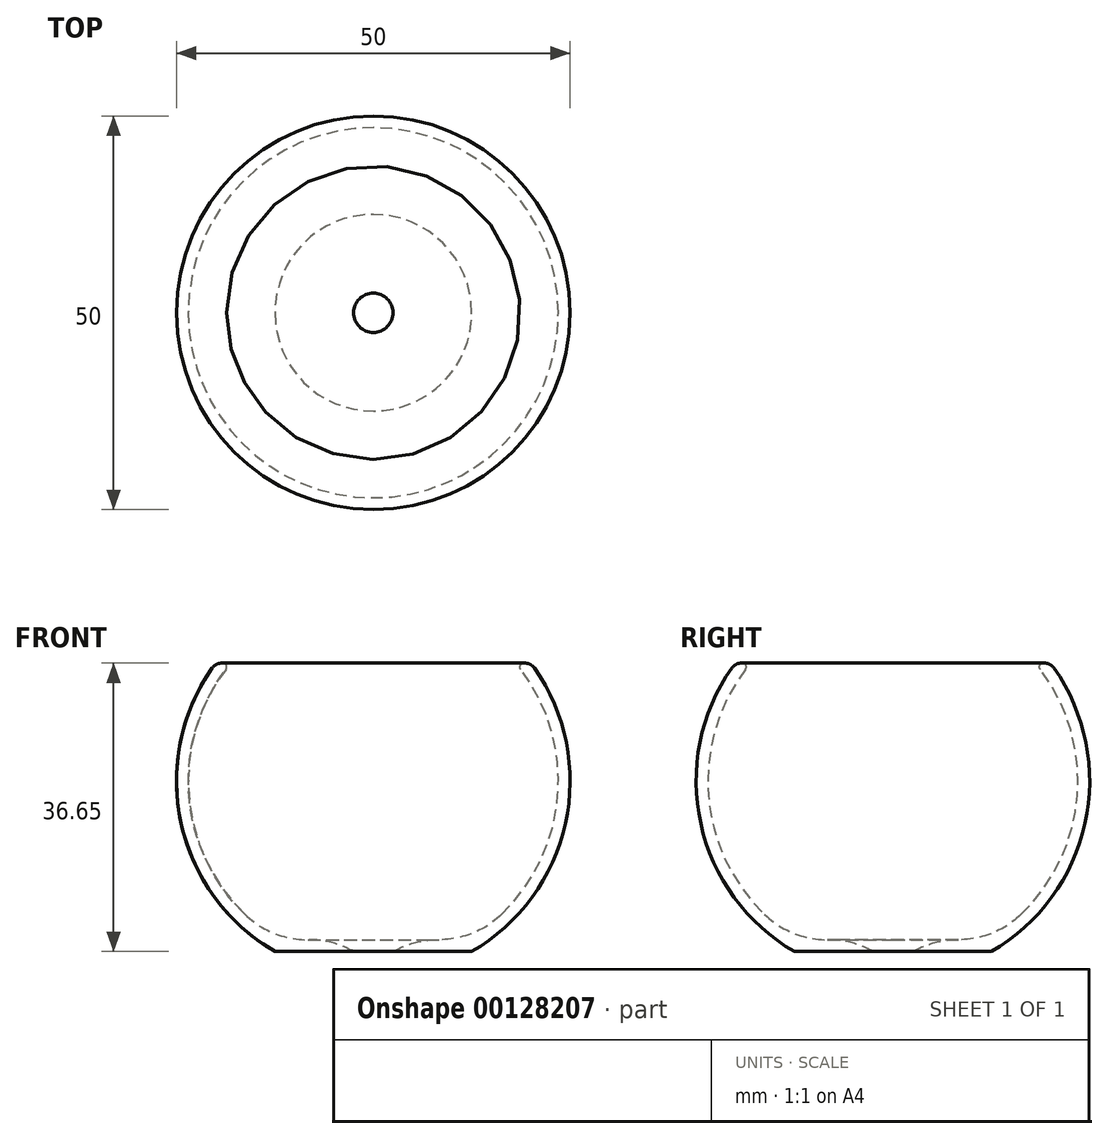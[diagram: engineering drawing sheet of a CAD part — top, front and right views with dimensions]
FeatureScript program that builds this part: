
annotation { "Feature Type Name" : "Feature", "Feature Type Description" : "" }
export const myFeature = defineFeature(function(context is Context, id is Id, definition is map)
    precondition{}
    {
        {
            var Q0;
            Q0=qCreatedBy(makeId("Front.planeOp"),FACE);
            var sketch = newSketch(context, id + "F0", { "sketchPlane" : qUnion([Q0])});
            skLineSegment(sketch, "E0", {"start": v(-12.5, -21.65) * mm, "end": v(0, -21.65) * mm});
            skLineSegment(sketch, "E1", {"start": v(-20, 15) * mm, "end": v(0, 15) * mm});
            skArc(sketch, "E2.trimOffspring", {"start": v(-20, 15) * mm, "mid": v(-24.5, -5.01) * mm, "end": v(-12.5, -21.65) * mm});
            skLineSegment(sketch, "E3", {"start": v(0, 15) * mm, "end": v(0, -21.65) * mm});
            skPoint(sketch, "E4.orphan", {"position": v(0, 43.43) * mm});
            skSolve(sketch);
        }
        {
            var Q0;
            Q0=makeQuery(id+"F0.imprint","IMPRINT",FACE,{"disambiguationData":[TD([[makeQuery(id+"F0.imprint","IMPRINT",EDGE,{"derivedFrom":sQuery(id+"F0.wireOp",EDGE,"E0")}),1.0]])]});
            var Q1;
            Q1=sQuery(id+"F0.wireOp",EDGE,"E3");
            revolve(context, id + "F1", {"entities" : qUnion([Q0]), "axis" : qUnion([Q1]), "revolveType" : RevolveType.FULL});
        }
        {
            var Q0;
            Q0=makeQuery(id+"F1.opRevolve","SWEPT_FACE",FACE,{"disambiguationData":[OSD([sQuery(id+"F0.wireOp",EDGE,"E1")])]});
            shell(context, id + "F2", {"entities" : qUnion([Q0]), "thickness" : 1.5 * mm});
        }
        {
            var Q0;
            Q0=makeQuery(id+"F2.opShell","OFFSET_FACE",FACE,{"disambiguationData":[OSD([sQuery(id+"F0.wireOp",EDGE,"E0")])]});
            var sketch = newSketch(context, id + "F3", { "sketchPlane" : qUnion([Q0])});
            skCircle(sketch, "E5", {"center": v(0, 0) * mm, "radius": 2 * mm});
            skSolve(sketch);
        }
        {
            var Q0;
            Q0=sQuery(id+"F3.wireOp",VERTEX,"E5.center");
            var Q1;
            Q1=makeQuery(id+"F1.opRevolve","SWEPT_BODY",BODY,{"disambiguationData":[OSD([sQuery(id+"F0.wireOp",EDGE,"E0"),sQuery(id+"F0.wireOp",EDGE,"E1"),sQuery(id+"F0.wireOp",EDGE,"E2.trimOffspring"),sQuery(id+"F0.wireOp",EDGE,"E3")])]});
            hole(context, id + "F4", {"style" : HoleStyle.SIMPLE, "endStyle" : HoleEndStyle.THROUGH, "holeDiameter" : 5 * mm, "locations" : qUnion([Q0]), "scope" : qUnion([Q1]), "isTappedThrough" : true});
        }
        {
            var Q0;
            Q0=makeQuery(id+"F2.opShell","OFFSET_FACE",FACE,{"disambiguationData":[OSD([sQuery(id+"F0.wireOp",EDGE,"E0")])]});
            fillet(context, id + "F5", {"entities" : qUnion([Q0]), "radius" : 11.5 * mm, "tangentPropagation" : true, "allowEdgeOverflow" : false});
        }
        {
            var Q0;
            Q0=makeQuery(id+"F2.opShell","OFFSET_EDGE",EDGE,{"disambiguationData":[OSD([sQuery(id+"F0.wireOp",EDGE,"E1"),sQuery(id+"F0.wireOp",EDGE,"E2.trimOffspring")])]});
            fillet(context, id + "F6", {"entities" : qUnion([Q0]), "radius" : 0.5 * mm, "tangentPropagation" : true, "allowEdgeOverflow" : false});
        }
        {
            var Q0;
            Q0=makeQuery(id+"F1.opRevolve","SWEPT_EDGE",EDGE,{"disambiguationData":[OSD([sQuery(id+"F0.wireOp",EDGE,"E1"),sQuery(id+"F0.wireOp",EDGE,"E2.trimOffspring")])]});
            var Q1;
            {var subQ0=sQuery(id+"F0.wireOp",EDGE,"E1");Q1=makeQuery(id+"F6.opFillet","BLEND_EDGE",EDGE,{"blendedFrom":[makeQuery(id+"F2.opShell","OFFSET_EDGE",EDGE,{"disambiguationData":[OSD([subQ0,sQuery(id+"F0.wireOp",EDGE,"E2.trimOffspring")])]}),makeQuery(id+"F1.opRevolve","SWEPT_FACE",FACE,{"disambiguationData":[OSD([subQ0])]})],"blendedInto":[makeQuery(id+"F1.opRevolve","SWEPT_FACE",FACE,{"disambiguationData":[OSD([subQ0])]})]});}
            fillet(context, id + "F7", {"entities" : qUnion([Q0, Q1]), "radius" : 1.5 * mm, "tangentPropagation" : true, "allowEdgeOverflow" : false});
        }
    });
